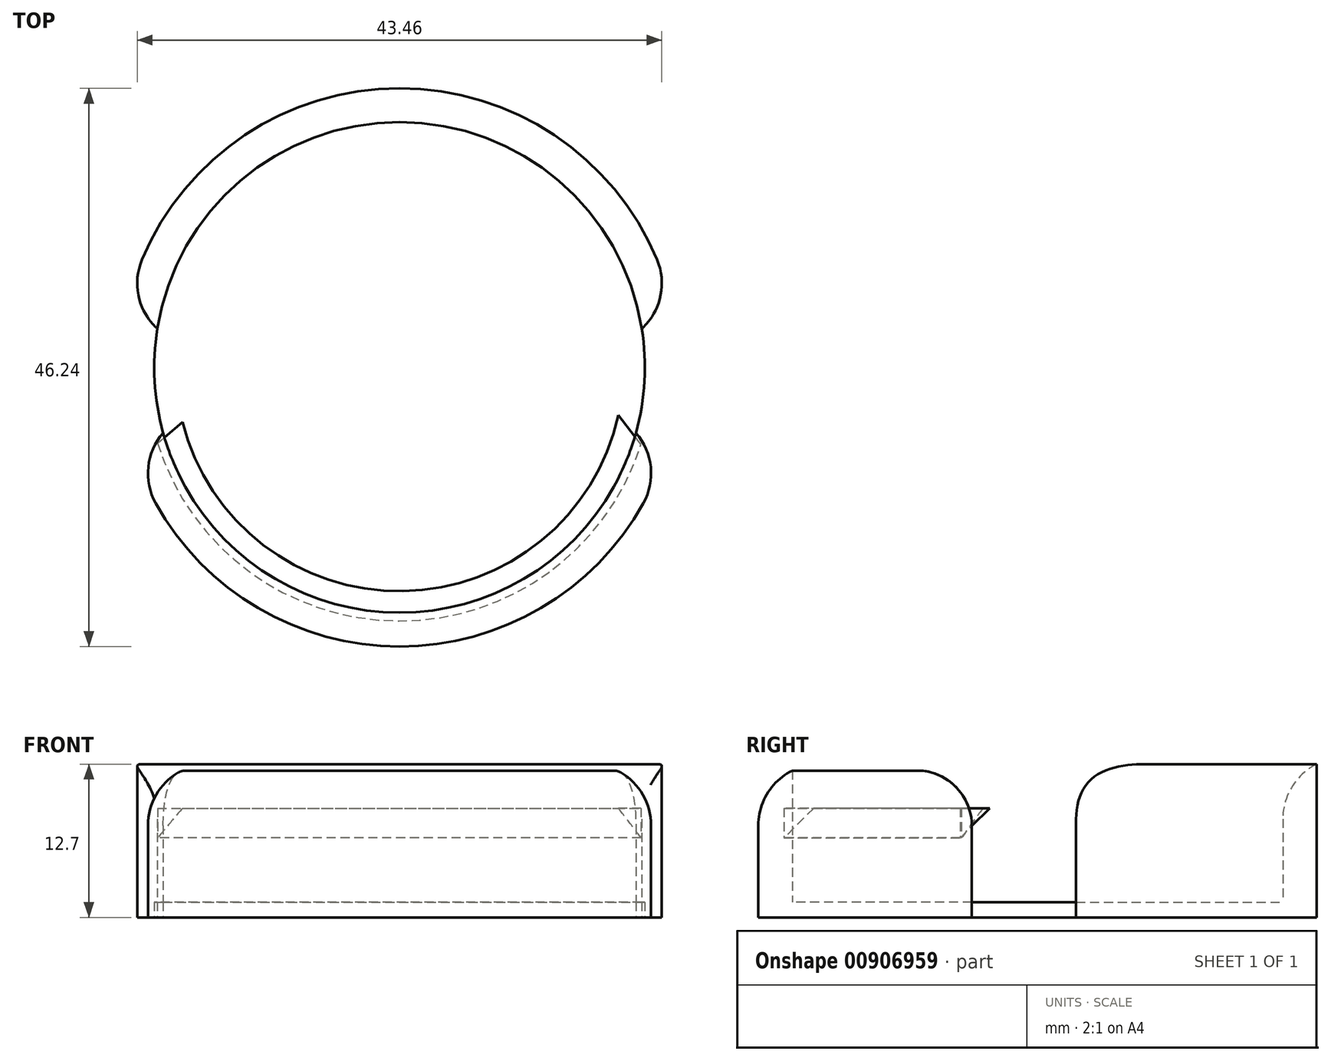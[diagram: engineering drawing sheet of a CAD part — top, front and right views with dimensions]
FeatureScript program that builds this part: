
annotation { "Feature Type Name" : "Feature", "Feature Type Description" : "" }
export const myFeature = defineFeature(function(context is Context, id is Id, definition is map)
    precondition{}
    {
        {
            var Q0;
            Q0=qCreatedBy(makeId("Top.planeOp"),FACE);
            var sketch = newSketch(context, id + "F0", { "sketchPlane" : qUnion([Q0])});
            skCircle(sketch, "E0", {"center": v(0, 0) * mm, "radius": 20.32 * mm});
            skArc(sketch, "E1", {"start": v(-22.48, -5.44) * mm, "mid": v(0, -23.12) * mm, "end": v(22.48, -5.44) * mm});
            skLineSegment(sketch, "E2", {"start": v(-22.9, 3.2) * mm, "end": v(-20.07, 3.2) * mm});
            skLineSegment(sketch, "E3", {"start": v(20.07, 3.2) * mm, "end": v(22.9, 3.2) * mm});
            skLineSegment(sketch, "E4", {"start": v(-22.48, -5.44) * mm, "end": v(-19.58, -5.44) * mm});
            skLineSegment(sketch, "E5", {"start": v(19.58, -5.44) * mm, "end": v(22.48, -5.44) * mm});
            skArc(sketch, "E6.trimOffspring", {"start": v(22.9, 3.2) * mm, "mid": v(0, 23.12) * mm, "end": v(-22.9, 3.2) * mm});
            skSolve(sketch);
        }
        {
            var Q0;
            {var subQ0=sQuery(id+"F0.wireOp",EDGE,"E0");var subQ1=makeQuery(id+"F0.imprint","INTERSECT",VERTEX,{"derivedFrom":[subQ0,sQuery(id+"F0.wireOp",EDGE,"E2")]});Q0=makeQuery(id+"F0.imprint","IMPRINT",FACE,{"disambiguationData":[TD([[makeQuery(id+"F0.imprint","IMPRINT",EDGE,{"disambiguationData":[TD([[subQ1,1.0]])],"derivedFrom":subQ0}),1.0]])]});}
            extrude(context, id + "F1", {"entities" : qUnion([Q0]), "depth" : 1.27 * mm, "offsetDistance" : 25.4 * mm});
        }
        {
            var Q0;
            {var subQ0=sQuery(id+"F0.wireOp",EDGE,"E2");Q0=makeQuery(id+"F0.imprint","IMPRINT",FACE,{"disambiguationData":[TD([[makeQuery(id+"F0.imprint","IMPRINT",EDGE,{"derivedFrom":subQ0}),1.0]])]});}
            extrude(context, id + "F2", {"entities" : qUnion([Q0]), "operationType" : NewBodyOperationType.ADD, "depth" : 12.7 * mm, "offsetDistance" : 25.4 * mm});
        }
        {
            var Q0;
            Q0=makeQuery(id+"F0.imprint","IMPRINT",FACE,{"disambiguationData":[TD([[makeQuery(id+"F0.imprint","IMPRINT",EDGE,{"derivedFrom":sQuery(id+"F0.wireOp",EDGE,"E1")}),1.0]])]});
            extrude(context, id + "F3", {"entities" : qUnion([Q0]), "operationType" : NewBodyOperationType.ADD, "depth" : 12.7 * mm, "offsetDistance" : 25.4 * mm});
        }
        {
            var Q0;
            Q0=makeQuery(id+"F3.opExtrude","SWEPT_EDGE",EDGE,{"disambiguationData":[OSD([sQuery(id+"F0.wireOp",EDGE,"E1"),sQuery(id+"F0.wireOp",EDGE,"E4")])]});
            var Q1;
            Q1=makeQuery(id+"F2.opExtrude","SWEPT_EDGE",EDGE,{"disambiguationData":[OSD([sQuery(id+"F0.wireOp",EDGE,"E2"),sQuery(id+"F0.wireOp",EDGE,"E6.trimOffspring")])]});
            var Q2;
            Q2=makeQuery(id+"F3.opExtrude","SWEPT_EDGE",EDGE,{"disambiguationData":[OSD([sQuery(id+"F0.wireOp",EDGE,"E1"),sQuery(id+"F0.wireOp",EDGE,"E5")])]});
            var Q3;
            Q3=makeQuery(id+"F2.opExtrude","SWEPT_EDGE",EDGE,{"disambiguationData":[OSD([sQuery(id+"F0.wireOp",EDGE,"E3"),sQuery(id+"F0.wireOp",EDGE,"E6.trimOffspring")])]});
            fillet(context, id + "F4", {"entities" : qUnion([Q0, Q1, Q2, Q3]), "radius" : 5.08 * mm, "tangentPropagation" : true, "allowEdgeOverflow" : false});
        }
        {
            var Q0;
            Q0=makeQuery(id+"F2.opExtrude","CAP_EDGE",EDGE,{"disambiguationData":[OSD([sQuery(id+"F0.wireOp",EDGE,"E0")])],"isStart":false});
            var Q1;
            Q1=makeQuery(id+"F3.opExtrude","CAP_EDGE",EDGE,{"disambiguationData":[OSD([sQuery(id+"F0.wireOp",EDGE,"E1")])],"isStart":false});
            fillet(context, id + "F5", {"entities" : qUnion([Q0, Q1]), "radius" : 5.08 * mm, "tangentPropagation" : true, "allowEdgeOverflow" : false});
        }
        {
            var Q0;
            Q0=qCreatedBy(makeId("Top.planeOp"),FACE);
            var sketch = newSketch(context, id + "F6", { "sketchPlane" : qUnion([Q0])});
            skArc(sketch, "E7", {"start": v(-20.04, -6.3) * mm, "mid": v(-0.05, -21) * mm, "end": v(20.01, -6.39) * mm});
            skArc(sketch, "E8", {"start": v(-17.99, -4.52) * mm, "mid": v(0.29, -18.54) * mm, "end": v(18.12, -3.96) * mm});
            skLineSegment(sketch, "E9", {"start": v(-20.04, -6.3) * mm, "end": v(-17.99, -4.52) * mm});
            skLineSegment(sketch, "E10", {"start": v(20.01, -6.39) * mm, "end": v(18.12, -3.96) * mm});
            skSolve(sketch);
        }
        {
            var Q0;
            Q0 = qSketchRegion(id + "F6", true);
            var Q1;
            Q1 = qConstructionFilter(qBodyType(qCreatedBy(id + "F6" ,EDGE), BodyType.WIRE), ConstructionObject.NO);
            extrude(context, id + "F7", {"entities" : qUnion([Q0]), "surfaceOperationType" : NewSurfaceOperationType.ADD, "surfaceEntities" : qUnion([Q1]), "endBound" : BoundingType.SYMMETRIC, "depth" : 2.54 * mm, "offsetDistance" : 25.4 * mm, "hasSecondDirection" : true, "secondDirectionOppositeDirection" : true, "secondDirectionDepth" : 25.4 * mm});
        }
        {
            var Q0;
            Q0=makeQuery(id+"F7.opExtrude","SWEPT_BODY",BODY,{"disambiguationData":[OSD([sQuery(id+"F6.wireOp",EDGE,"E10")])]});
            transform(context, id + "F8", {"entities" : qUnion([Q0]), "transformType" : TransformType.TRANSLATION_3D, "dx" : 0 * mm, "dy" : 0 * mm, "dz" : 7.77 * mm, "makeCopy" : false});
        }
        {
            var Q0;
            Q0=makeQuery(id+"F7.opExtrude","CAP_EDGE",EDGE,{"disambiguationData":[OSD([sQuery(id+"F6.wireOp",EDGE,"E8")])],"isStart":true});
            chamfer(context, id + "F9", {"entities" : qUnion([Q0]), "width" : 2.54 * mm, "tangentPropagation" : true});
        }
    });
